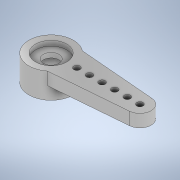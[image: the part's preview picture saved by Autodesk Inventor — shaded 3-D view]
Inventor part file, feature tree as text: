
AUTODESK INVENTOR PART (.ipt)
format: ipt  version: 2020 (Build 240168000, 168)  size: 144,384 bytes
history: mixed  units: in
note: dims shown in document units (in); Inventor stores cm internally (conversion verified against a paired STEP export)
features: mirror x1, imported_body x1
ambient origin geometry x8: Origin, YZ Plane, XZ Plane, XY Plane, X Axis, Y Axis, Z Axis, Center Point
bodies: Solid1 (imported_parasolid)
feature tree (2):
  mirror  "Mirror1"
  imported_body  NMx_Import_Brep_tag  [imported B-rep: ~18 faces, bbox_mm=[14.232466, 4.0, 6.31]]
